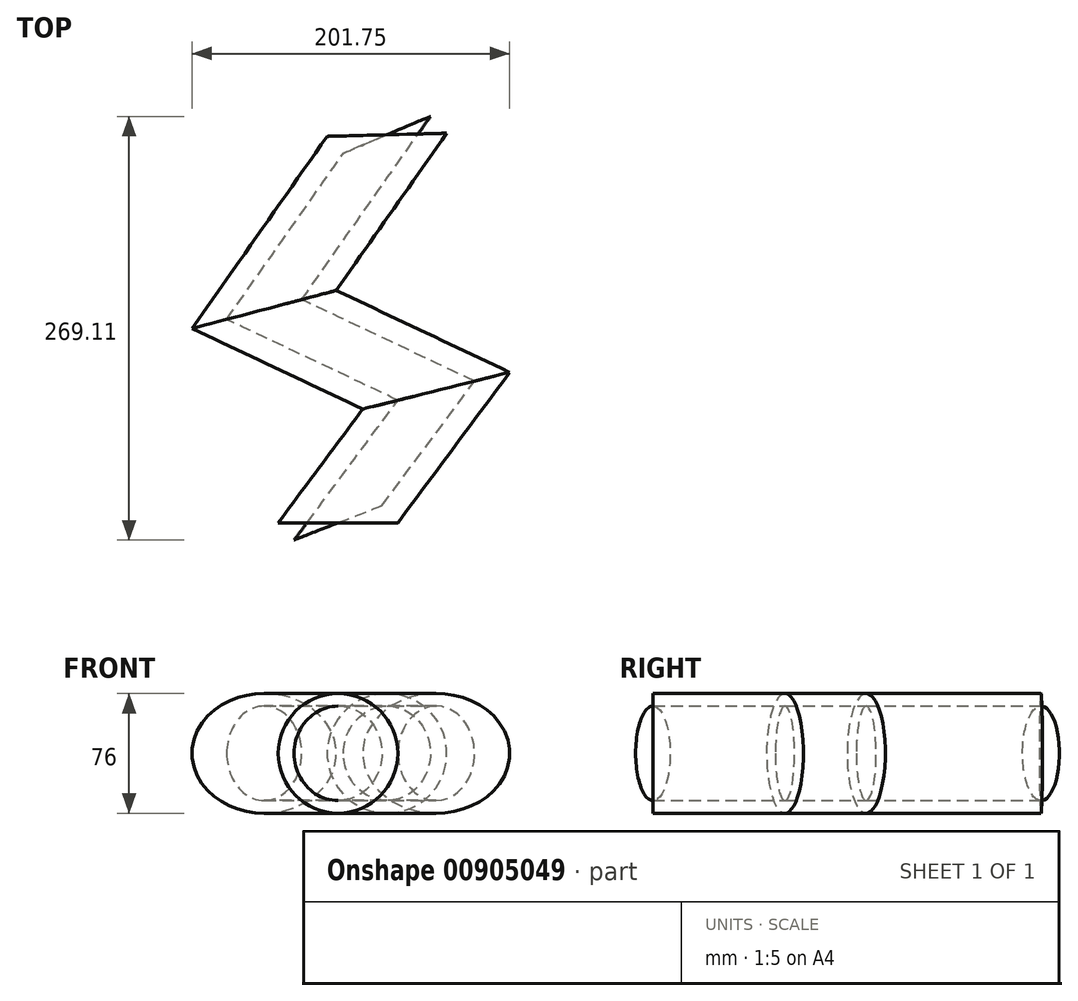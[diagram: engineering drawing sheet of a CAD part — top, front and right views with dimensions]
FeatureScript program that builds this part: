
annotation { "Feature Type Name" : "Feature", "Feature Type Description" : "" }
export const myFeature = defineFeature(function(context is Context, id is Id, definition is map)
    precondition{}
    {
        {
            var Q0;
            Q0=qCreatedBy(makeId("Front.planeOp"),FACE);
            var sketch = newSketch(context, id + "F0", { "sketchPlane" : qUnion([Q0])});
            skCircle(sketch, "E0", {"center": v(0, 0) * mm, "radius": 38 * mm});
            skSolve(sketch);
        }
        {
            var Q0;
            Q0=qCreatedBy(makeId("Top.planeOp"),FACE);
            var sketch = newSketch(context, id + "F1", { "sketchPlane" : qUnion([Q0])});
            skLineSegment(sketch, "E1", {"start": v(-44.88, 214.3) * mm, "end": v(63.1, 260.02) * mm});
            skSolve(sketch);
        }
        {
            var Q0;
            Q0=sQuery(id+"F1.wireOp",EDGE,"E1");
            cPlane(context, id + "F2", {"entities" : qUnion([Q0]), "cplaneType" : CPlaneType.LINE_ANGLE, "offset" : 25 * mm, "angle" : 0 * degree, "width" : 150 * mm, "height" : 150 * mm});
        }
        {
            var Q0;
            Q0=qCreatedBy(id+"F2.planeOp",FACE);
            var sketch = newSketch(context, id + "F3", { "sketchPlane" : qUnion([Q0])});
            skCircle(sketch, "E2", {"center": v(-124.69, 0) * mm, "radius": 30 * mm});
            skSolve(sketch);
        }
        {
            var Q0;
            Q0=qCreatedBy(makeId("Top.planeOp"),FACE);
            var sketch = newSketch(context, id + "F4", { "sketchPlane" : qUnion([Q0])});
            skLineSegment(sketch, "E3", {"start": v(31.04, 246.46) * mm, "end": v(-46.94, 135.48) * mm});
            skLineSegment(sketch, "E4", {"start": v(-46.94, 135.48) * mm, "end": v(62.33, 83.9) * mm});
            skLineSegment(sketch, "E5", {"start": v(62.33, 83.9) * mm, "end": v(0, 0) * mm});
            skSolve(sketch);
        }
        {
            var Q0;
            Q0=makeQuery(id+"F3.imprint","IMPRINT",FACE,{"disambiguationData":[TD([[makeQuery(id+"F3.imprint","IMPRINT",EDGE,{"derivedFrom":sQuery(id+"F3.wireOp",EDGE,"E2")}),1.0]])]});
            var Q1;
            Q1=makeQuery(id+"F0.imprint","IMPRINT",FACE,{"disambiguationData":[TD([[makeQuery(id+"F0.imprint","IMPRINT",EDGE,{"derivedFrom":sQuery(id+"F0.wireOp",EDGE,"E0")}),1.0]])]});
            var Q2;
            Q2=sQuery(id+"F4.wireOp",EDGE,"E3");
            var Q3;
            Q3=sQuery(id+"F4.wireOp",EDGE,"E4");
            var Q4;
            Q4=sQuery(id+"F4.wireOp",EDGE,"E5");
            sweep(context, id + "F5", {"profiles" : qUnion([Q0, Q1]), "path" : qUnion([Q2, Q3, Q4])});
        }
    });
